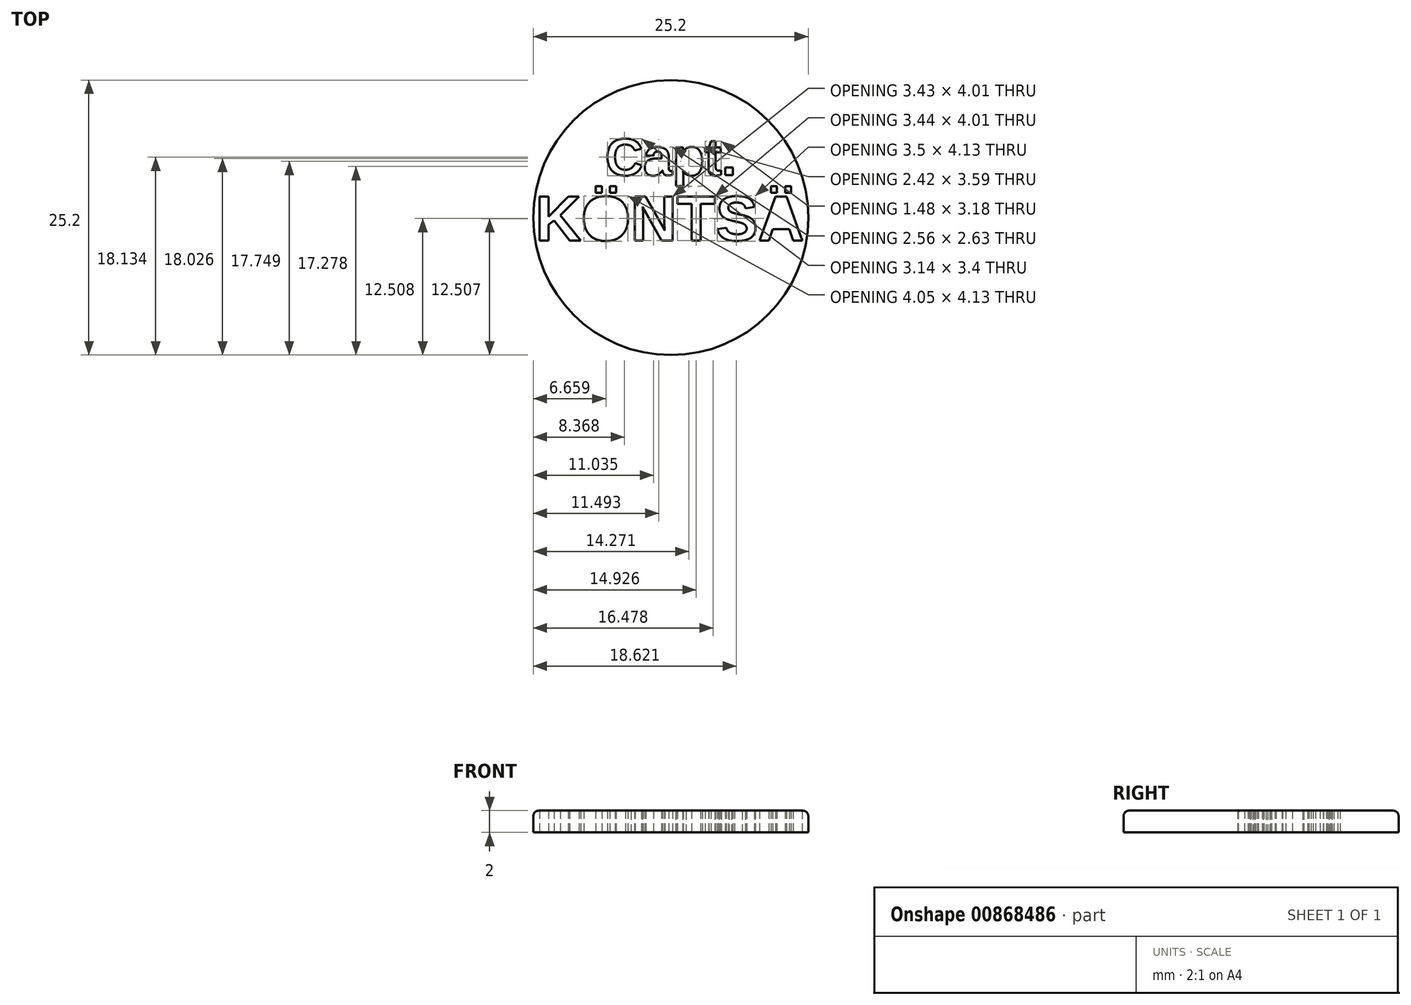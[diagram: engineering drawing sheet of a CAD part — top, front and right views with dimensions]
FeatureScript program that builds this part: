
annotation { "Feature Type Name" : "Feature", "Feature Type Description" : "" }
export const myFeature = defineFeature(function(context is Context, id is Id, definition is map)
    precondition{}
    {
        {
            var Q0;
            Q0=qCreatedBy(makeId("Top.planeOp"),FACE);
            var sketch = newSketch(context, id + "F0", { "sketchPlane" : qUnion([Q0])});
            skCircle(sketch, "E0", {"center": v(0, 0) * mm, "radius": 12.6 * mm});
            skText(sketch, "E1", { "text": "KÖNTSÄ", "fontName": "Arimo-Bold.ttf"});
            skText(sketch, "E2", { "text": "Capt.", "fontName": "Arimo-Bold.ttf"});
            const initialGuessF0  = {"E1": [-0.01242, -0.0021, 1, 0, 0.0042], "E2": [-0.006, 0.00388, 1, 0, 0.00346]};
            skSetInitialGuess(sketch, initialGuessF0);
            skSolve(sketch);
        }
        {
            var Q0;
            Q0=makeQuery(id+"F0.imprint","IMPRINT",FACE,{"disambiguationData":[TD([[makeQuery(id+"F0.imprint","IMPRINT",EDGE,{"derivedFrom":sQuery(id+"F0.wireOp",EDGE,"E0")}),1.0]])]});
            extrude(context, id + "F1", {"entities" : qUnion([Q0]), "depth" : 2 * mm, "offsetDistance" : 25 * mm});
        }
        {
            var Q0;
            Q0=makeQuery(id+"F1.opExtrude","CAP_EDGE",EDGE,{"disambiguationData":[OSD([sQuery(id+"F0.wireOp",EDGE,"E0")])],"isStart":false});
            fillet(context, id + "F2", {"entities" : qUnion([Q0]), "radius" : 0.5 * mm, "tangentPropagation" : true, "allowEdgeOverflow" : false});
        }
    });
